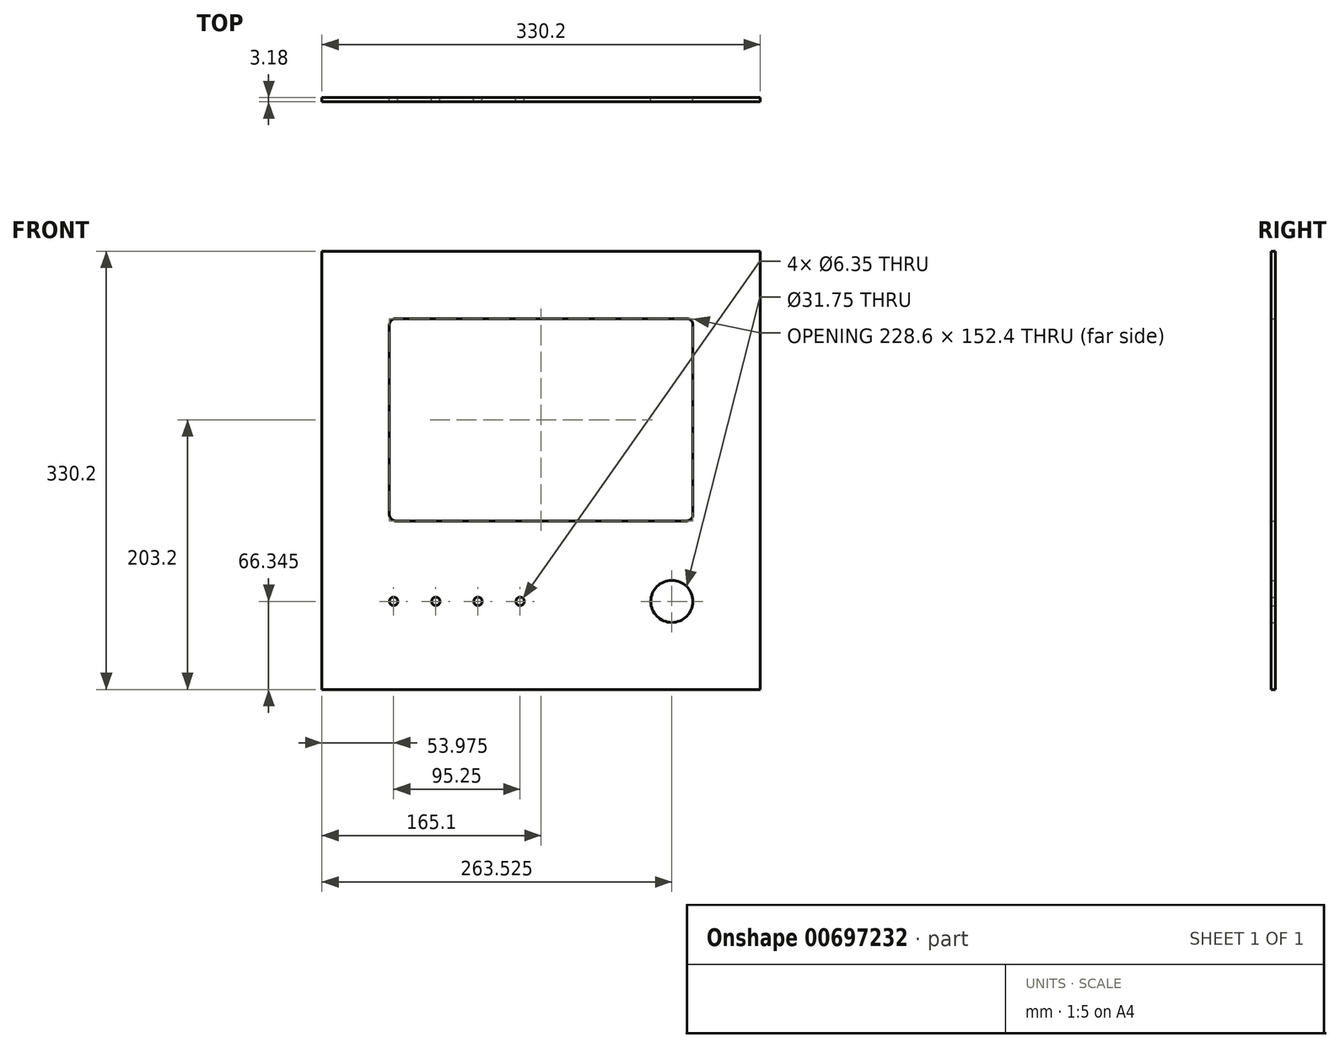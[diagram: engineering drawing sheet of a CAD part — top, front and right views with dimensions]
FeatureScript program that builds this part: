
annotation { "Feature Type Name" : "Feature", "Feature Type Description" : "" }
export const myFeature = defineFeature(function(context is Context, id is Id, definition is map)
    precondition{}
    {
        {
            var Q0;
            Q0=qCreatedBy(makeId("Front.planeOp"),FACE);
            var sketch = newSketch(context, id + "F0", { "sketchPlane" : qUnion([Q0])});
            skLineSegment(sketch, "E0.bottom", {"start": v(-165.1, -165.1) * mm, "end": v(165.1, -165.1) * mm});
            skLineSegment(sketch, "E0.top", {"start": v(-165.1, 165.1) * mm, "end": v(165.1, 165.1) * mm});
            skLineSegment(sketch, "E0.left", {"start": v(-165.1, -165.1) * mm, "end": v(-165.1, 165.1) * mm});
            skLineSegment(sketch, "E0.right", {"start": v(165.1, -165.1) * mm, "end": v(165.1, 165.1) * mm});
            skPoint(sketch, "E0.middle", {"position": v(0, 0) * mm});
            skSolve(sketch);
        }
        {
            var Q0;
            Q0=makeQuery(id+"F0.imprint","IMPRINT",FACE,{"disambiguationData":[TD([[makeQuery(id+"F0.imprint","IMPRINT",EDGE,{"derivedFrom":sQuery(id+"F0.wireOp",EDGE,"E0.bottom")}),1.0]])]});
            var sketch = newSketch(context, id + "F1", { "sketchPlane" : qUnion([Q0])});
            skLineSegment(sketch, "E1.bottom", {"start": v(-109.54, -38.1) * mm, "end": v(109.54, -38.1) * mm});
            skLineSegment(sketch, "E1.top", {"start": v(-109.54, 114.3) * mm, "end": v(109.54, 114.3) * mm});
            skLineSegment(sketch, "E1.left", {"start": v(-114.3, -33.34) * mm, "end": v(-114.3, 109.54) * mm});
            skLineSegment(sketch, "E1.right", {"start": v(114.3, -33.34) * mm, "end": v(114.3, 109.54) * mm});
            skPoint(sketch, "E1.middle", {"position": v(0, 76.2) * mm});
            skPoint(sketch, "E2.visualSharp", {"position": v(-114.3, 114.3) * mm});
            skArc(sketch, "E2.filletArc", {"start": v(-109.54, 114.3) * mm, "mid": v(-112.9, 112.9) * mm, "end": v(-114.3, 109.54) * mm});
            skPoint(sketch, "E3.visualSharp", {"position": v(-114.3, -38.1) * mm});
            skArc(sketch, "E3.filletArc", {"start": v(-114.3, -33.34) * mm, "mid": v(-112.9, -36.7) * mm, "end": v(-109.54, -38.1) * mm});
            skPoint(sketch, "E4.visualSharp", {"position": v(114.3, -38.1) * mm});
            skArc(sketch, "E4.filletArc", {"start": v(109.54, -38.1) * mm, "mid": v(112.9, -36.7) * mm, "end": v(114.3, -33.34) * mm});
            skPoint(sketch, "E5.visualSharp", {"position": v(114.3, 114.3) * mm});
            skArc(sketch, "E5.filletArc", {"start": v(114.3, 109.54) * mm, "mid": v(112.9, 112.9) * mm, "end": v(109.54, 114.3) * mm});
            skSolve(sketch);
        }
        {
            var Q0;
            Q0=makeQuery(id+"F0.imprint","IMPRINT",FACE,{"disambiguationData":[TD([[makeQuery(id+"F0.imprint","IMPRINT",EDGE,{"derivedFrom":sQuery(id+"F0.wireOp",EDGE,"E0.bottom")}),1.0]])]});
            var sketch = newSketch(context, id + "F2", { "sketchPlane" : qUnion([Q0])});
            skCircle(sketch, "E6", {"center": v(98.43, -98.75) * mm, "radius": 15.88 * mm});
            skLineSegment(sketch, "E7", {"start": v(98.43, -98.75) * mm, "end": v(-114.3, -98.75) * mm});
            skCircle(sketch, "E8", {"center": v(-111.12, -98.75) * mm, "radius": 3.18 * mm});
            skCircle(sketch, "E9", {"center": v(-79.38, -98.75) * mm, "radius": 3.18 * mm});
            skCircle(sketch, "E10", {"center": v(-47.62, -98.75) * mm, "radius": 3.18 * mm});
            skCircle(sketch, "E11", {"center": v(-15.88, -98.75) * mm, "radius": 3.18 * mm});
            skSolve(sketch);
        }
        {
            var Q0;
            Q0 = qSketchRegion(id + "F0", true);
            extrude(context, id + "F3", {"entities" : qUnion([Q0]), "depth" : 3.17 * mm, "offsetDistance" : 25.4 * mm});
        }
        {
            var Q0;
            Q0=makeQuery(id+"F1.imprint","IMPRINT",FACE,{"disambiguationData":[TD([[makeQuery(id+"F1.imprint","IMPRINT",EDGE,{"derivedFrom":sQuery(id+"F1.wireOp",EDGE,"E1.bottom")}),1.0]])]});
            var Q1;
            Q1=makeQuery(id+"F2.imprint","IMPRINT",FACE,{"disambiguationData":[TD([[makeQuery(id+"F2.imprint","IMPRINT",EDGE,{"derivedFrom":sQuery(id+"F2.wireOp",EDGE,"E6")}),1.0]])]});
            var Q2;
            {var subQ0=sQuery(id+"F2.wireOp",EDGE,"E11");var subQ1=sQuery(id+"F2.wireOp",EDGE,"E7");var subQ2=makeQuery(id+"F2.imprint","INTERSECT",VERTEX,{"disambiguationData":[OD(0.0)],"derivedFrom":[subQ1,subQ0]});Q2=makeQuery(id+"F2.imprint","IMPRINT",FACE,{"disambiguationData":[TD([[makeQuery(id+"F2.imprint","IMPRINT",EDGE,{"disambiguationData":[TD([[subQ2,1.0]])],"derivedFrom":subQ1}),1.0]])]});}
            var Q3;
            {var subQ0=sQuery(id+"F2.wireOp",EDGE,"E11");var subQ1=sQuery(id+"F2.wireOp",EDGE,"E7");var subQ2=makeQuery(id+"F2.imprint","INTERSECT",VERTEX,{"disambiguationData":[OD(0.0)],"derivedFrom":[subQ1,subQ0]});Q3=makeQuery(id+"F2.imprint","IMPRINT",FACE,{"disambiguationData":[TD([[makeQuery(id+"F2.imprint","IMPRINT",EDGE,{"disambiguationData":[TD([[subQ2,1.0]])],"derivedFrom":subQ1}),-1.0]])]});}
            var Q4;
            {var subQ0=sQuery(id+"F2.wireOp",EDGE,"E10");var subQ1=sQuery(id+"F2.wireOp",EDGE,"E7");var subQ2=makeQuery(id+"F2.imprint","INTERSECT",VERTEX,{"disambiguationData":[OD(0.0)],"derivedFrom":[subQ1,subQ0]});Q4=makeQuery(id+"F2.imprint","IMPRINT",FACE,{"disambiguationData":[TD([[makeQuery(id+"F2.imprint","IMPRINT",EDGE,{"disambiguationData":[TD([[subQ2,1.0]])],"derivedFrom":subQ1}),-1.0]])]});}
            var Q5;
            {var subQ0=sQuery(id+"F2.wireOp",EDGE,"E10");var subQ1=sQuery(id+"F2.wireOp",EDGE,"E7");var subQ2=makeQuery(id+"F2.imprint","INTERSECT",VERTEX,{"disambiguationData":[OD(0.0)],"derivedFrom":[subQ1,subQ0]});Q5=makeQuery(id+"F2.imprint","IMPRINT",FACE,{"disambiguationData":[TD([[makeQuery(id+"F2.imprint","IMPRINT",EDGE,{"disambiguationData":[TD([[subQ2,1.0]])],"derivedFrom":subQ1}),1.0]])]});}
            var Q6;
            {var subQ0=sQuery(id+"F2.wireOp",EDGE,"E9");var subQ1=sQuery(id+"F2.wireOp",EDGE,"E7");var subQ2=makeQuery(id+"F2.imprint","INTERSECT",VERTEX,{"disambiguationData":[OD(0.0)],"derivedFrom":[subQ1,subQ0]});Q6=makeQuery(id+"F2.imprint","IMPRINT",FACE,{"disambiguationData":[TD([[makeQuery(id+"F2.imprint","IMPRINT",EDGE,{"disambiguationData":[TD([[subQ2,1.0]])],"derivedFrom":subQ1}),-1.0]])]});}
            var Q7;
            {var subQ0=sQuery(id+"F2.wireOp",EDGE,"E9");var subQ1=sQuery(id+"F2.wireOp",EDGE,"E7");var subQ2=makeQuery(id+"F2.imprint","INTERSECT",VERTEX,{"disambiguationData":[OD(0.0)],"derivedFrom":[subQ1,subQ0]});Q7=makeQuery(id+"F2.imprint","IMPRINT",FACE,{"disambiguationData":[TD([[makeQuery(id+"F2.imprint","IMPRINT",EDGE,{"disambiguationData":[TD([[subQ2,1.0]])],"derivedFrom":subQ1}),1.0]])]});}
            var Q8;
            {var subQ0=sQuery(id+"F2.wireOp",EDGE,"E8");var subQ1=sQuery(id+"F2.wireOp",EDGE,"E7");var subQ2=makeQuery(id+"F2.imprint","INTERSECT",VERTEX,{"disambiguationData":[OD(0.0)],"derivedFrom":[subQ1,subQ0]});Q8=makeQuery(id+"F2.imprint","IMPRINT",FACE,{"disambiguationData":[TD([[makeQuery(id+"F2.imprint","IMPRINT",EDGE,{"disambiguationData":[TD([[subQ2,1.0]])],"derivedFrom":subQ1}),1.0]])]});}
            var Q9;
            {var subQ0=sQuery(id+"F2.wireOp",EDGE,"E8");var subQ1=sQuery(id+"F2.wireOp",EDGE,"E7");var subQ2=makeQuery(id+"F2.imprint","INTERSECT",VERTEX,{"disambiguationData":[OD(0.0)],"derivedFrom":[subQ1,subQ0]});Q9=makeQuery(id+"F2.imprint","IMPRINT",FACE,{"disambiguationData":[TD([[makeQuery(id+"F2.imprint","IMPRINT",EDGE,{"disambiguationData":[TD([[subQ2,1.0]])],"derivedFrom":subQ1}),-1.0]])]});}
            extrude(context, id + "F4", {"entities" : qUnion([Q0, Q1, Q2, Q3, Q4, Q5, Q6, Q7, Q8, Q9]), "operationType" : NewBodyOperationType.REMOVE, "depth" : 25.4 * mm, "offsetDistance" : 25.4 * mm});
        }
    });
